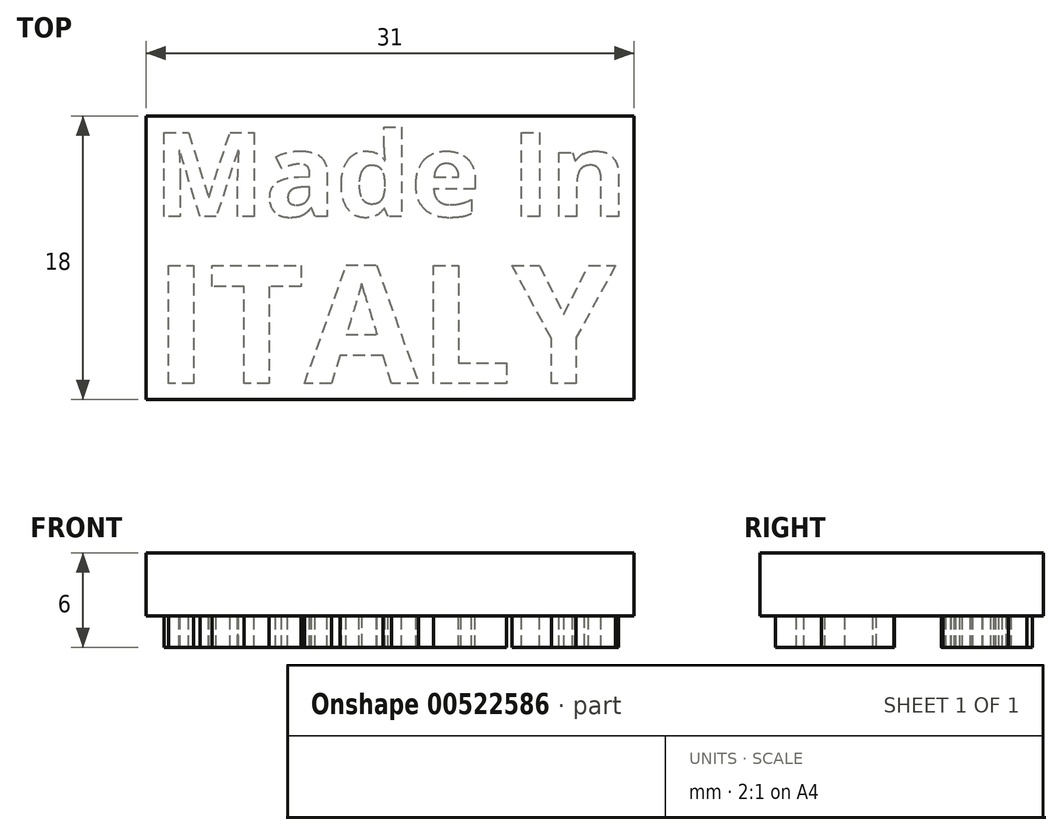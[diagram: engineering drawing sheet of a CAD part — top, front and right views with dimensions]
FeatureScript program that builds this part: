
annotation { "Feature Type Name" : "Feature", "Feature Type Description" : "" }
export const myFeature = defineFeature(function(context is Context, id is Id, definition is map)
    precondition{}
    {
        {
            var Q0;
            Q0=qCreatedBy(makeId("Top.planeOp"),FACE);
            var sketch = newSketch(context, id + "F0", { "sketchPlane" : qUnion([Q0])});
            skLineSegment(sketch, "E0.bottom", {"start": v(15, 8) * mm, "end": v(-15, 8) * mm, "construction": true});
            skLineSegment(sketch, "E0.top", {"start": v(15, -8) * mm, "end": v(-15, -8) * mm, "construction": true});
            skLineSegment(sketch, "E0.left", {"start": v(15, 8) * mm, "end": v(15, -8) * mm, "construction": true});
            skLineSegment(sketch, "E0.right", {"start": v(-15, 8) * mm, "end": v(-15, -8) * mm, "construction": true});
            skPoint(sketch, "E0.middle", {"position": v(0, 0) * mm});
            skText(sketch, "E1", { "text": "Made In", "fontName": "OpenSans-Bold.ttf"});
            skText(sketch, "E2", { "text": "ITALY", "fontName": "OpenSans-Bold.ttf"});
            skLineSegment(sketch, "E3.top", {"start": v(-15, -8) * mm, "end": v(15, -8) * mm, "construction": true});
            const initialGuessF0  = {"E1": [-0.015, 0.00261, 1, 0, 0.00539], "E2": [-0.015, -0.008, 1, 0, 0.00757]};
            skSetInitialGuess(sketch, initialGuessF0);
            skSolve(sketch);
        }
        {
            var Q0;
            Q0=qCreatedBy(makeId("Top.planeOp"),FACE);
            var sketch = newSketch(context, id + "F1", { "sketchPlane" : qUnion([Q0])});
            skLineSegment(sketch, "E4.bottom", {"start": v(15.5, 9) * mm, "end": v(-15.5, 9) * mm});
            skLineSegment(sketch, "E4.top", {"start": v(15.5, -9) * mm, "end": v(-15.5, -9) * mm});
            skLineSegment(sketch, "E4.left", {"start": v(15.5, 9) * mm, "end": v(15.5, -9) * mm});
            skLineSegment(sketch, "E4.right", {"start": v(-15.5, 9) * mm, "end": v(-15.5, -9) * mm});
            skPoint(sketch, "E4.middle", {"position": v(0, 0) * mm});
            skSolve(sketch);
        }
        {
            var Q0;
            Q0 = qSketchRegion(id + "F1", true);
            extrude(context, id + "F2", {"entities" : qUnion([Q0]), "depth" : 4 * mm, "offsetDistance" : 25 * mm});
        }
        {
            var Q0;
            Q0=makeQuery(id+"F0.imprint","IMPRINT",FACE,{"disambiguationData":[TD([[makeQuery(id+"F0.imprint","IMPRINT",EDGE,{"derivedFrom":sQuery(id+"F0.wireOp",EDGE,"E2.sketch_text.stroke-30")}),-1.0]])]});
            var Q1;
            Q1=makeQuery(id+"F0.imprint","IMPRINT",FACE,{"disambiguationData":[TD([[makeQuery(id+"F0.imprint","IMPRINT",EDGE,{"derivedFrom":sQuery(id+"F0.wireOp",EDGE,"E2.sketch_text.stroke-24")}),-1.0]])]});
            var Q2;
            Q2=makeQuery(id+"F0.imprint","IMPRINT",FACE,{"disambiguationData":[TD([[makeQuery(id+"F0.imprint","IMPRINT",EDGE,{"derivedFrom":sQuery(id+"F0.wireOp",EDGE,"E2.sketch_text.stroke-12")}),-1.0]])]});
            var Q3;
            Q3=makeQuery(id+"F0.imprint","IMPRINT",FACE,{"disambiguationData":[TD([[makeQuery(id+"F0.imprint","IMPRINT",EDGE,{"derivedFrom":sQuery(id+"F0.wireOp",EDGE,"E2.sketch_text.stroke-4")}),-1.0]])]});
            var Q4;
            Q4=makeQuery(id+"F0.imprint","IMPRINT",FACE,{"disambiguationData":[TD([[makeQuery(id+"F0.imprint","IMPRINT",EDGE,{"derivedFrom":sQuery(id+"F0.wireOp",EDGE,"E2.sketch_text.stroke-0")}),-1.0]])]});
            extrude(context, id + "F3", {"entities" : qUnion([Q0, Q1, Q2, Q3, Q4]), "operationType" : NewBodyOperationType.ADD, "oppositeDirection" : true, "depth" : 2 * mm, "offsetDistance" : 25 * mm});
        }
        {
            var Q0;
            Q0=makeQuery(id+"F0.imprint","IMPRINT",FACE,{"disambiguationData":[TD([[makeQuery(id+"F0.imprint","IMPRINT",EDGE,{"derivedFrom":sQuery(id+"F0.wireOp",EDGE,"E1.sketch_text.stroke-87")}),-1.0]])]});
            var Q1;
            Q1=makeQuery(id+"F0.imprint","IMPRINT",FACE,{"disambiguationData":[TD([[makeQuery(id+"F0.imprint","IMPRINT",EDGE,{"derivedFrom":sQuery(id+"F0.wireOp",EDGE,"E1.sketch_text.stroke-91")}),-1.0]])]});
            var Q2;
            Q2=makeQuery(id+"F0.imprint","IMPRINT",FACE,{"disambiguationData":[TD([[makeQuery(id+"F0.imprint","IMPRINT",EDGE,{"derivedFrom":sQuery(id+"F0.wireOp",EDGE,"E1.sketch_text.stroke-67")}),-1.0]])]});
            var Q3;
            Q3=makeQuery(id+"F0.imprint","IMPRINT",FACE,{"disambiguationData":[TD([[makeQuery(id+"F0.imprint","IMPRINT",EDGE,{"derivedFrom":sQuery(id+"F0.wireOp",EDGE,"E1.sketch_text.stroke-44")}),-1.0]])]});
            var Q4;
            Q4=makeQuery(id+"F0.imprint","IMPRINT",FACE,{"disambiguationData":[TD([[makeQuery(id+"F0.imprint","IMPRINT",EDGE,{"derivedFrom":sQuery(id+"F0.wireOp",EDGE,"E1.sketch_text.stroke-19")}),-1.0]])]});
            var Q5;
            Q5=makeQuery(id+"F0.imprint","IMPRINT",FACE,{"disambiguationData":[TD([[makeQuery(id+"F0.imprint","IMPRINT",EDGE,{"derivedFrom":sQuery(id+"F0.wireOp",EDGE,"E1.sketch_text.stroke-0")}),-1.0]])]});
            extrude(context, id + "F4", {"entities" : qUnion([Q0, Q1, Q2, Q3, Q4, Q5]), "operationType" : NewBodyOperationType.ADD, "oppositeDirection" : true, "depth" : 2 * mm, "offsetDistance" : 25 * mm});
        }
    });
